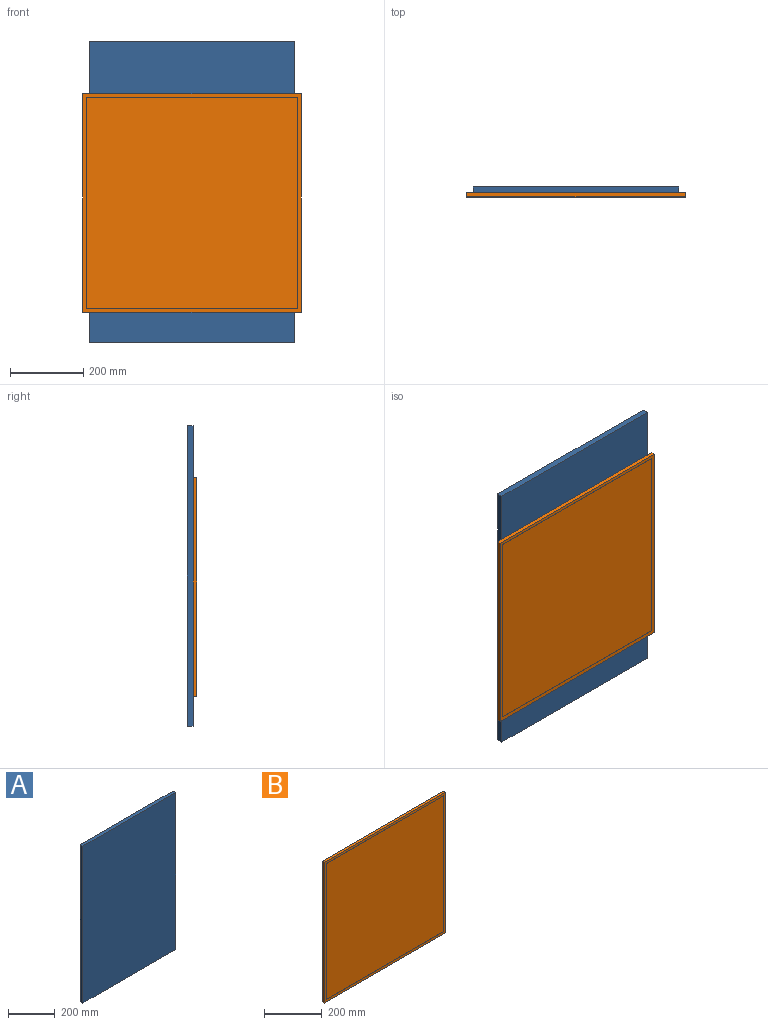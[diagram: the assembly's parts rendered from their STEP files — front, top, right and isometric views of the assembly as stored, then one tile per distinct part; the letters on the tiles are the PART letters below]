
ASSEMBLY  parts=2 mates=1
PART A: 6 faces, bbox 560x16x820 mm
  f0: plane 560x16mm, normal (0,0,1), area 8960mm2, adj f1,f3,f4,f5
  f1: plane 820x16mm, normal (-1,0,0), area 13120mm2, adj f0,f2,f4,f5
  f2: plane 560x16mm, normal (0,0,-1), area 8960mm2, adj f1,f3,f4,f5
  f3: plane 820x16mm, normal (1,0,0), area 13120mm2, adj f0,f2,f4,f5
  f4: plane 820x560mm, normal (0,-1,0), area 459200mm2, adj f0,f1,f2,f3
  f5: plane 820x560mm, normal (0,1,0), area 459200mm2, adj f0,f1,f2,f3
PART B: 11 faces, bbox 595x10.5x595 mm
  f0: plane 595x10.5mm, normal (1,0,0), area 6247.5mm2, adj f1,f3,f4,f5
  f1: plane 595x10.5mm, normal (0,0,1), area 6247.5mm2, adj f0,f2,f4,f5
  f2: plane 595x10.5mm, normal (-1,0,0), area 6247.5mm2, adj f1,f3,f4,f5
  f3: plane 595x10.5mm, normal (0,0,-1), area 6247.5mm2, adj f0,f2,f4,f5
  f4: plane 595x595mm, normal (0,1,0), area 354025mm2, adj f0,f1,f2,f3
  f5: plane 595x595mm, normal (0,-1,0), area 23400mm2, adj f0,f1,f2,f3,f6,f7,f8,f9
  f6: plane 575x1mm, normal (0,0,-1), area 575mm2, adj f5,f7,f9,f10
  f7: plane 575x1mm, normal (1,0,0), area 575mm2, adj f5,f6,f8,f10
  f8: plane 575x1mm, normal (0,0,1), area 575mm2, adj f5,f7,f9,f10
  f9: plane 575x1mm, normal (-1,0,0), area 575mm2, adj f5,f6,f8,f10
  f10: plane 575x575mm, normal (0,-1,0), area 330625mm2, adj f6,f7,f8,f9
PLACE A t=(-3345,0,-605)mm
PLACE B t=(0,-26.5,-30)mm
MATE fastened B.f4 <-> A.f4  axis (0,1,0) through (0,-16,-30)mm
